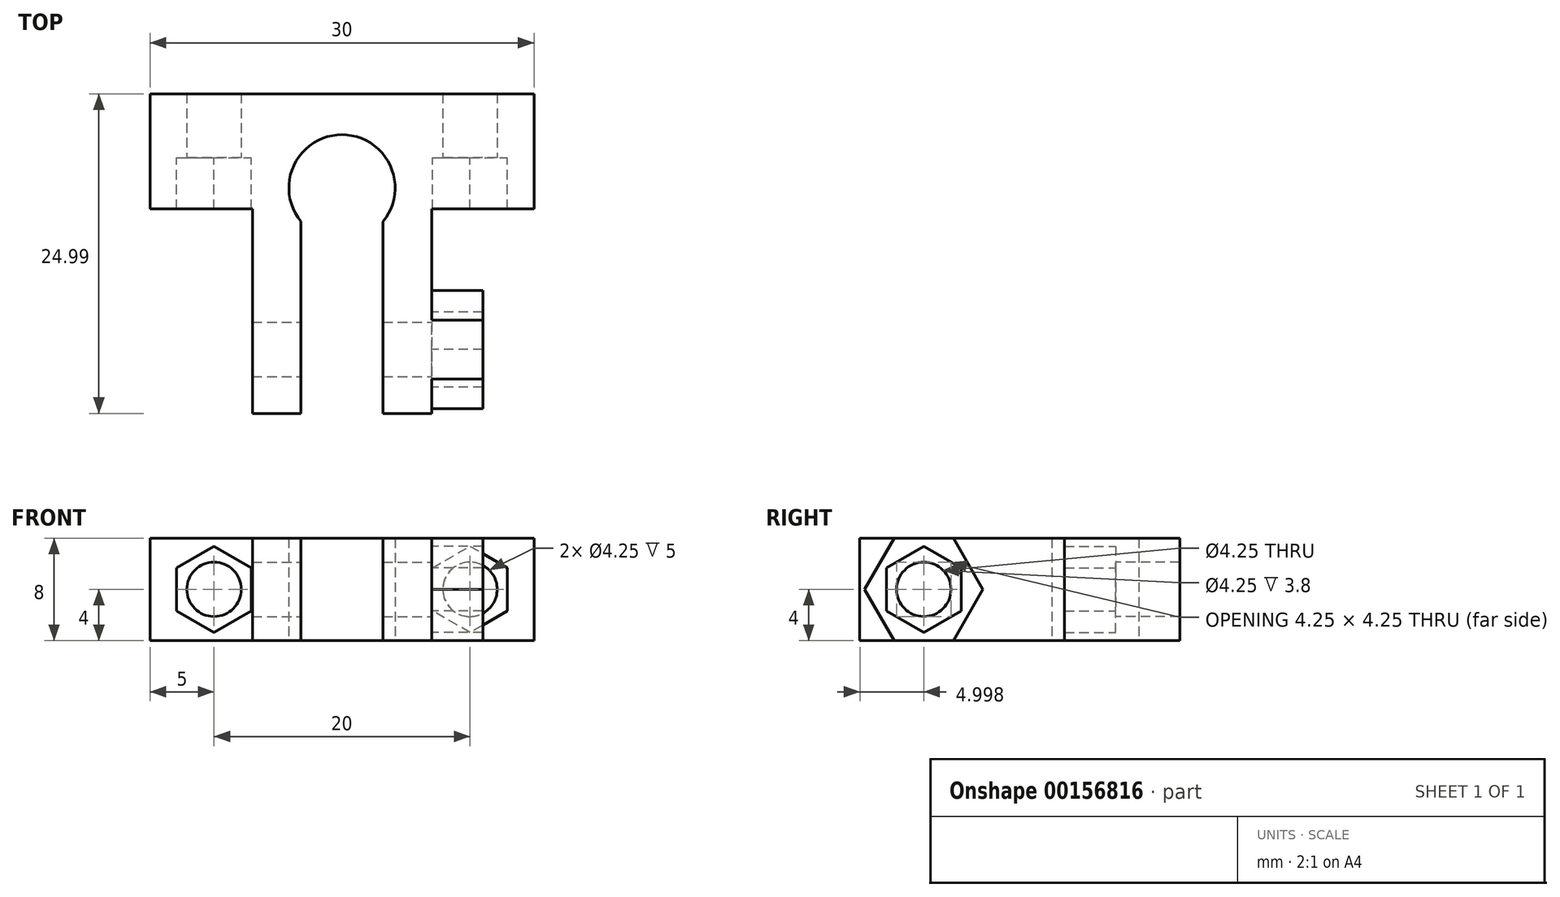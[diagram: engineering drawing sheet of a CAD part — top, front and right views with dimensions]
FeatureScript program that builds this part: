
annotation { "Feature Type Name" : "Feature", "Feature Type Description" : "" }
export const myFeature = defineFeature(function(context is Context, id is Id, definition is map)
    precondition{}
    {
        {
            var Q0;
            Q0=qCreatedBy(makeId("Top.planeOp"),FACE);
            var sketch = newSketch(context, id + "F0", { "sketchPlane" : qUnion([Q0])});
            skArc(sketch, "E0", {"start": v(3.2, -2.64) * mm, "mid": v(0, 4.15) * mm, "end": v(-3.2, -2.64) * mm});
            skLineSegment(sketch, "E1", {"start": v(-3.2, -2.64) * mm, "end": v(-3.2, -17.64) * mm});
            skLineSegment(sketch, "E2", {"start": v(-3.2, -17.64) * mm, "end": v(-7, -17.64) * mm});
            skLineSegment(sketch, "E3", {"start": v(-7, -17.64) * mm, "end": v(-7, 2.35) * mm});
            skLineSegment(sketch, "E4", {"start": v(-7, 2.35) * mm, "end": v(-15, 2.35) * mm});
            skLineSegment(sketch, "E5", {"start": v(-15, 2.35) * mm, "end": v(-15, 7.35) * mm});
            skLineSegment(sketch, "E6", {"start": v(-15, 7.35) * mm, "end": v(15, 7.35) * mm});
            skLineSegment(sketch, "E7", {"start": v(15, 7.35) * mm, "end": v(15, 2.35) * mm});
            skLineSegment(sketch, "E8", {"start": v(15, 2.35) * mm, "end": v(7, 2.35) * mm});
            skLineSegment(sketch, "E9", {"start": v(7, 2.35) * mm, "end": v(7, -17.64) * mm});
            skLineSegment(sketch, "E10", {"start": v(7, -17.64) * mm, "end": v(3.2, -17.64) * mm});
            skLineSegment(sketch, "E11", {"start": v(3.2, -17.64) * mm, "end": v(3.2, -2.64) * mm});
            skLineSegment(sketch, "E12", {"start": v(0, 4.15) * mm, "end": v(0, 7.35) * mm, "construction": true});
            skSolve(sketch);
        }
        {
            var Q0;
            Q0=qSketchRegion(id+"F0",true);
            extrude(context, id + "F1", {"entities" : qUnion([Q0]), "endBound" : BoundingType.SYMMETRIC, "depth" : 8 * mm});
        }
        {
            var Q0;
            Q0=makeQuery(id+"F1.opExtrude","SWEPT_FACE",FACE,{"disambiguationData":[OSD([sQuery(id+"F0.wireOp",EDGE,"E8")])]});
            var sketch = newSketch(context, id + "F2", { "sketchPlane" : qUnion([Q0])});
            skCircle(sketch, "E13", {"center": v(10, 0) * mm, "radius": 2.12 * mm});
            skCircle(sketch, "E14.MirrorC", {"center": v(-10, 0) * mm, "radius": 2.12 * mm});
            skSolve(sketch);
        }
        {
            var Q0;
            Q0=qSketchRegion(id+"F2",true);
            extrude(context, id + "F3", {"entities" : qUnion([Q0]), "operationType" : NewBodyOperationType.REMOVE, "endBound" : BoundingType.THROUGH_ALL, "oppositeDirection" : true, "depth" : 25 * mm});
        }
        {
            var Q0;
            Q0=makeQuery(id+"F1.opExtrude","SWEPT_FACE",FACE,{"disambiguationData":[OSD([sQuery(id+"F0.wireOp",EDGE,"E8")])]});
            var sketch = newSketch(context, id + "F4", { "sketchPlane" : qUnion([Q0])});
            skCircle(sketch, "E15.cCircle", {"center": v(10, 0) * mm, "radius": 2.93 * mm, "construction": true});
            skLineSegment(sketch, "E15.0", {"start": v(12.92, 1.69) * mm, "end": v(12.92, -1.69) * mm});
            skLineSegment(sketch, "E15.1", {"start": v(12.92, -1.69) * mm, "end": v(10, -3.38) * mm});
            skLineSegment(sketch, "E15.2", {"start": v(10, -3.38) * mm, "end": v(7.07, -1.69) * mm});
            skLineSegment(sketch, "E15.3", {"start": v(7.07, -1.69) * mm, "end": v(7.07, 1.69) * mm});
            skLineSegment(sketch, "E15.4", {"start": v(7.07, 1.69) * mm, "end": v(10, 3.38) * mm});
            skLineSegment(sketch, "E15.5", {"start": v(10, 3.38) * mm, "end": v(12.92, 1.69) * mm});
            skPoint(sketch, "E15.0.midPoint", {"position": v(12.92, 0) * mm});
            skLineSegment(sketch, "E16.MirrorCS", {"start": v(-7.07, -1.69) * mm, "end": v(-7.07, 1.69) * mm});
            skPoint(sketch, "E17.MirrorP", {"position": v(-12.92, 0) * mm});
            skCircle(sketch, "E18.MirrorC", {"center": v(-10, 0) * mm, "radius": 2.93 * mm, "construction": true});
            skLineSegment(sketch, "E19.MirrorCS", {"start": v(-12.92, 1.69) * mm, "end": v(-12.92, -1.69) * mm});
            skLineSegment(sketch, "E20.MirrorCS", {"start": v(-12.92, -1.69) * mm, "end": v(-10, -3.38) * mm});
            skLineSegment(sketch, "E21.MirrorCS", {"start": v(-10, -3.38) * mm, "end": v(-7.07, -1.69) * mm});
            skLineSegment(sketch, "E22.MirrorCS", {"start": v(-7.07, 1.69) * mm, "end": v(-10, 3.38) * mm});
            skLineSegment(sketch, "E23.MirrorCS", {"start": v(-10, 3.38) * mm, "end": v(-12.92, 1.69) * mm});
            skLineSegment(sketch, "E24.bottom", {"start": v(15, 4) * mm, "end": v(7, 4) * mm});
            skLineSegment(sketch, "E24.top", {"start": v(15, -4) * mm, "end": v(7, -4) * mm});
            skLineSegment(sketch, "E24.left", {"start": v(15, 4) * mm, "end": v(15, -4) * mm});
            skLineSegment(sketch, "E24.right", {"start": v(7, 4) * mm, "end": v(7, -4) * mm});
            skLineSegment(sketch, "E25.MirrorCS", {"start": v(-1, 4) * mm, "end": v(7, 4) * mm});
            skLineSegment(sketch, "E26.MirrorCS", {"start": v(-7, 4) * mm, "end": v(-7, -4) * mm});
            skLineSegment(sketch, "E27.MirrorCS", {"start": v(-15, 4) * mm, "end": v(-7, 4) * mm});
            skLineSegment(sketch, "E28.MirrorCS", {"start": v(-15, 4) * mm, "end": v(-15, -4) * mm});
            skLineSegment(sketch, "E29.MirrorCS", {"start": v(-15, -4) * mm, "end": v(-7, -4) * mm});
            skSolve(sketch);
        }
        {
            var Q0;
            Q0=qSketchRegion(id+"F4",true);
            extrude(context, id + "F5", {"entities" : qUnion([Q0]), "operationType" : NewBodyOperationType.ADD, "depth" : 4 * mm});
        }
        {
            var Q0;
            Q0=makeQuery(id+"F1.opExtrude","SWEPT_FACE",FACE,{"disambiguationData":[OSD([sQuery(id+"F0.wireOp",EDGE,"E9")])]});
            var sketch = newSketch(context, id + "F6", { "sketchPlane" : qUnion([Q0])});
            skCircle(sketch, "E30", {"center": v(-12.64, 0) * mm, "radius": 2.12 * mm});
            skSolve(sketch);
        }
        {
            var Q0;
            Q0=qSketchRegion(id+"F6",true);
            extrude(context, id + "F7", {"entities" : qUnion([Q0]), "operationType" : NewBodyOperationType.REMOVE, "endBound" : BoundingType.THROUGH_ALL, "oppositeDirection" : true, "depth" : 25 * mm});
        }
        {
            var Q0;
            Q0=makeQuery(id+"F1.opExtrude","SWEPT_FACE",FACE,{"disambiguationData":[OSD([sQuery(id+"F0.wireOp",EDGE,"E9")])]});
            var sketch = newSketch(context, id + "F8", { "sketchPlane" : qUnion([Q0])});
            skCircle(sketch, "E31.cCircle", {"center": v(-12.64, 0) * mm, "radius": 2.93 * mm, "construction": true});
            skLineSegment(sketch, "E31.0", {"start": v(-9.72, 1.69) * mm, "end": v(-9.72, -1.69) * mm});
            skLineSegment(sketch, "E31.1", {"start": v(-9.72, -1.69) * mm, "end": v(-12.64, -3.38) * mm});
            skLineSegment(sketch, "E31.2", {"start": v(-12.64, -3.38) * mm, "end": v(-15.57, -1.69) * mm});
            skLineSegment(sketch, "E31.3", {"start": v(-15.57, -1.69) * mm, "end": v(-15.57, 1.69) * mm});
            skLineSegment(sketch, "E31.4", {"start": v(-15.57, 1.69) * mm, "end": v(-12.64, 3.38) * mm});
            skLineSegment(sketch, "E31.5", {"start": v(-12.64, 3.38) * mm, "end": v(-9.72, 1.69) * mm});
            skPoint(sketch, "E31.0.midPoint", {"position": v(-9.72, 0) * mm});
            skCircle(sketch, "E32.cCircle", {"center": v(-12.64, 0) * mm, "radius": 4 * mm, "construction": true});
            skLineSegment(sketch, "E32.0", {"start": v(-10.33, -4) * mm, "end": v(-14.95, -4) * mm});
            skLineSegment(sketch, "E32.1", {"start": v(-14.95, -4) * mm, "end": v(-17.26, 0) * mm});
            skLineSegment(sketch, "E32.2", {"start": v(-17.26, 0) * mm, "end": v(-14.95, 4) * mm});
            skLineSegment(sketch, "E32.3", {"start": v(-14.95, 4) * mm, "end": v(-10.33, 4) * mm});
            skLineSegment(sketch, "E32.4", {"start": v(-10.33, 4) * mm, "end": v(-8.02, 0) * mm});
            skLineSegment(sketch, "E32.5", {"start": v(-8.02, 0) * mm, "end": v(-10.33, -4) * mm});
            skPoint(sketch, "E32.0.midPoint", {"position": v(-12.64, -4) * mm});
            skSolve(sketch);
        }
        {
            var Q0;
            Q0=qSketchRegion(id+"F8",true);
            extrude(context, id + "F9", {"entities" : qUnion([Q0]), "operationType" : NewBodyOperationType.ADD, "depth" : 4 * mm});
        }
    });
